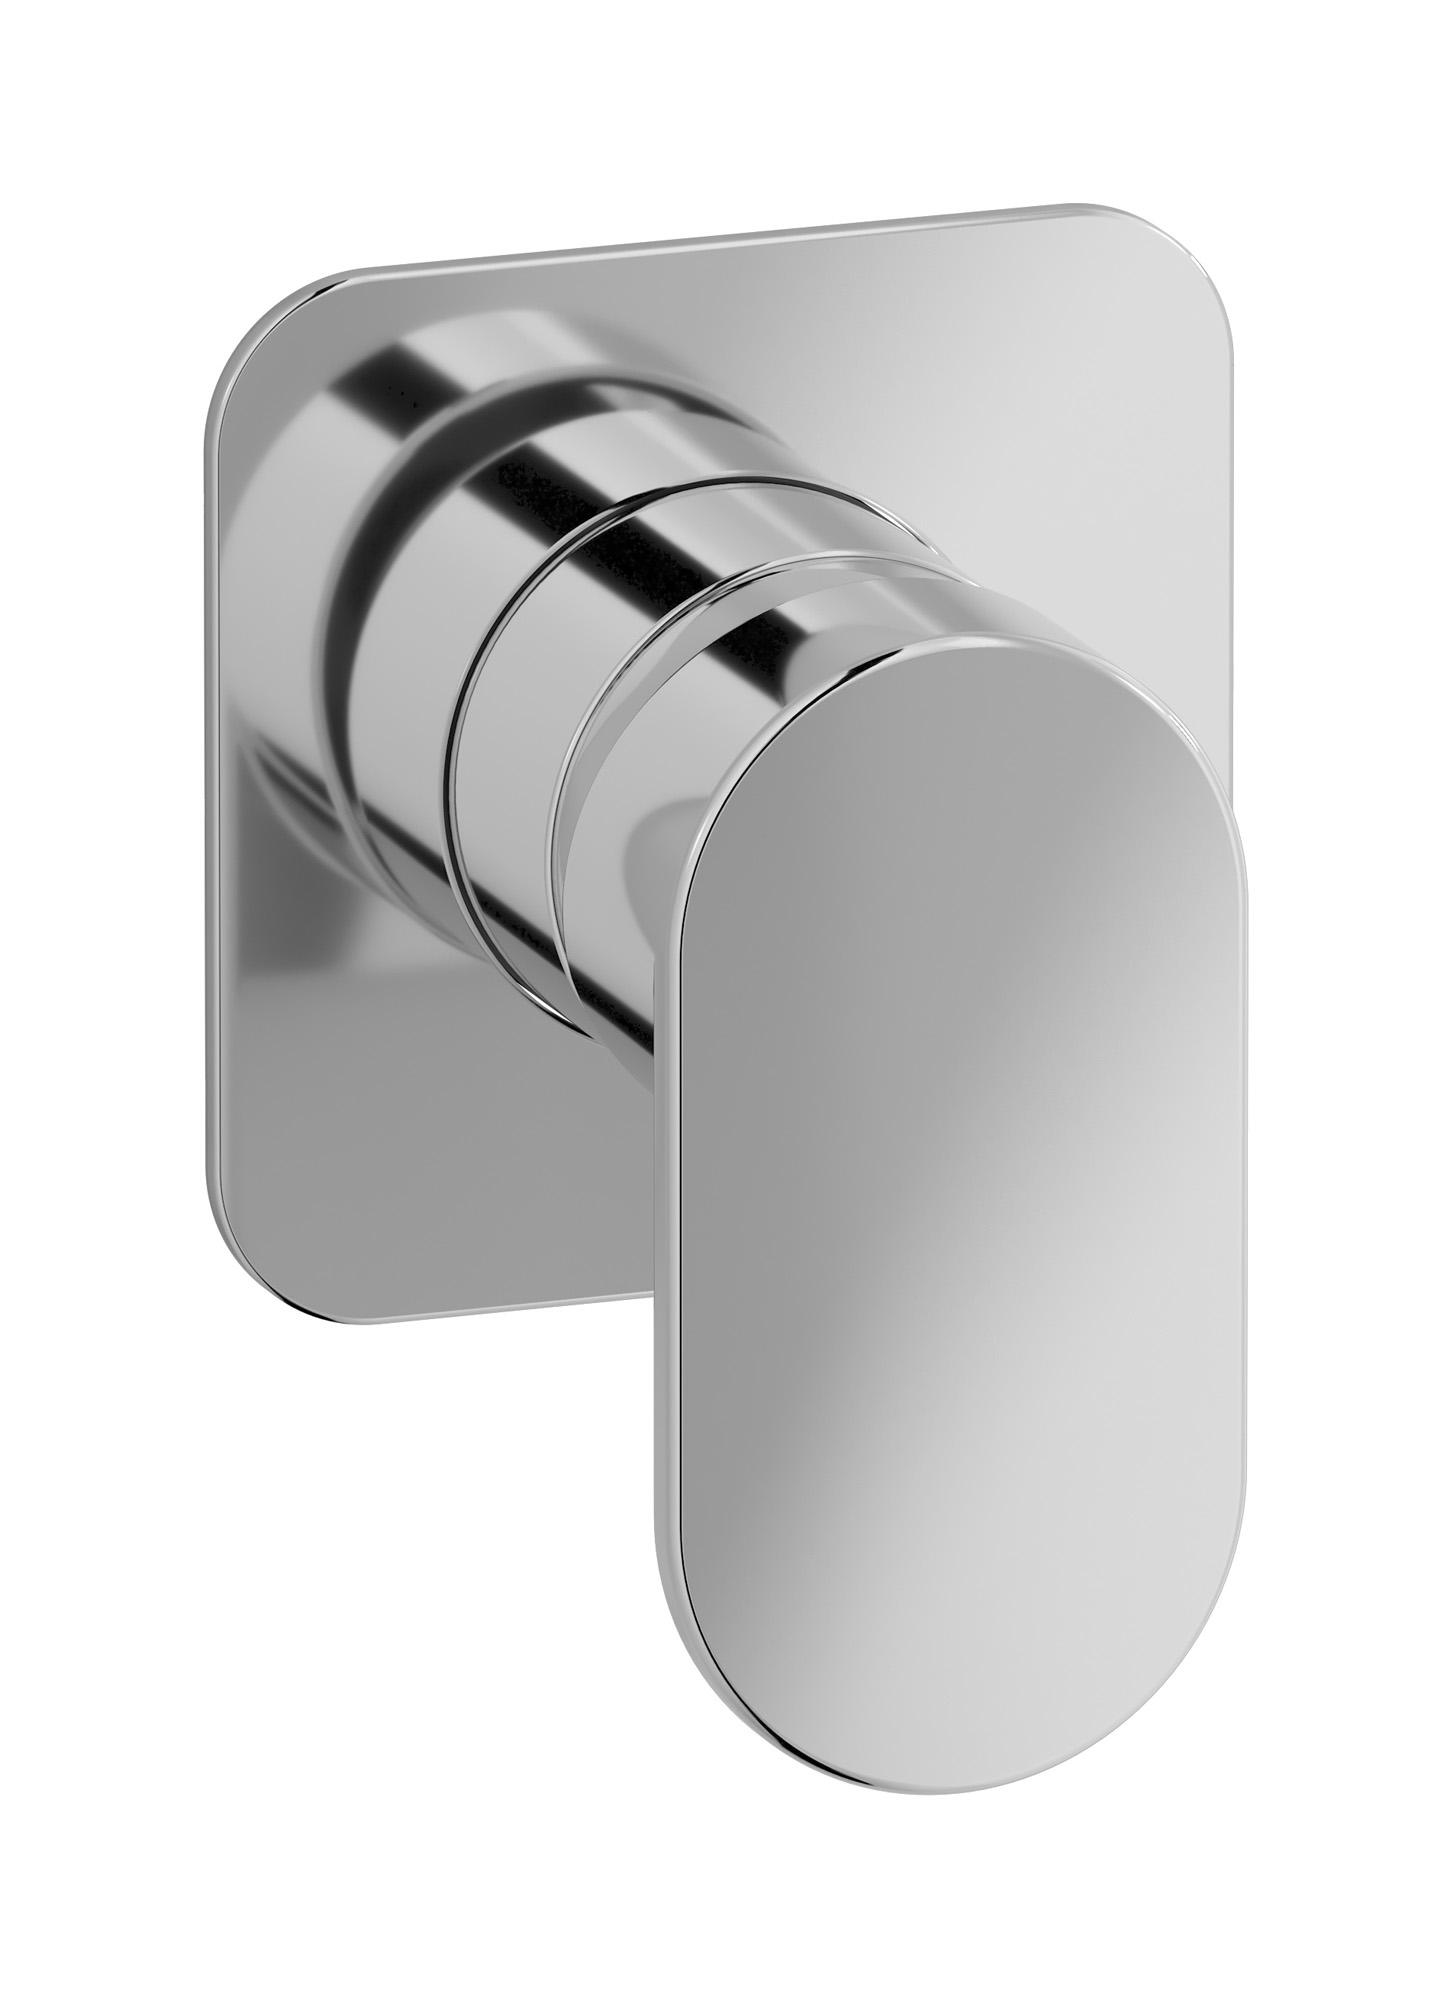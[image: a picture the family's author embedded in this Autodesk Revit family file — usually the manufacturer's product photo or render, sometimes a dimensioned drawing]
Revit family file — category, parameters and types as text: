
# Revit family: LM300
name_source: partatom
category: Apparecchi idraulici
units: mm (PartAtom-declared; Revit-internal decimal feet)

## family parameters
Basato su piano di lavoro = No
Condiviso = No
Mantieni orientamento annotazione = No
Numero OmniClass = 23.45.55.17
Punto di calcolo locali = No
Quota connettore circolare = Usa diametro
Sempre verticale = Sì
Taglio con vuoti quando caricato = No
Tipo di parte = Normale
Titolo OmniClass = Mixing Faucets

## types (9) — shared parameters
Cold water inlet = 10 mm  [stored 0.0328084 ft]
Commenti sul tipo = Wall mixer
Connessione CW = No
Connessione HW = No
Connessione di scarico = No
Connessione di ventilazione = No
Descrizione = Exposed parts for manual wall mixer
Hot water inlet = 10 mm  [stored 0.0328084 ft]
Produttore = IB Rubinetterie S.p.A.
URL = https://www.weareib.it
zero-valued in all types: Prospetto di default

## per-type parameters (varying)
| type | Finishes surface | Immagine tipo | Modello |
| Chrome | IB_Chrome | LM300CC.jpg | LM300CC |
| Brushed nickel | IB_Brushed nickel | LM300SS.jpg | LM300SS |
| Matt white | IB_matt white | LM300BO.jpg | LM300BO |
| Matt black | IB_matt black | LM300NP.jpg | LM300NP |
| Natural brass | IB_Brass | LM300ON.jpg | LM300ON |
| Brushed black chrome | IB_Brushed black chrome | LM300CS.jpg | LM300CS |
| Brushed rose gold | IB_Brushed rose gold | LM300SR.jpg | LM300SR |
| Brushed gold | IB_brushed gold | LM300OS.jpg | LM300OS |
| Brushed pale gold | IB_brushed pale gold | LM300IS.jpg | LM300IS |

note: [stored X ft] marks values corroborated as IEEE doubles in the binary element streams (Revit-internal decimal feet)
